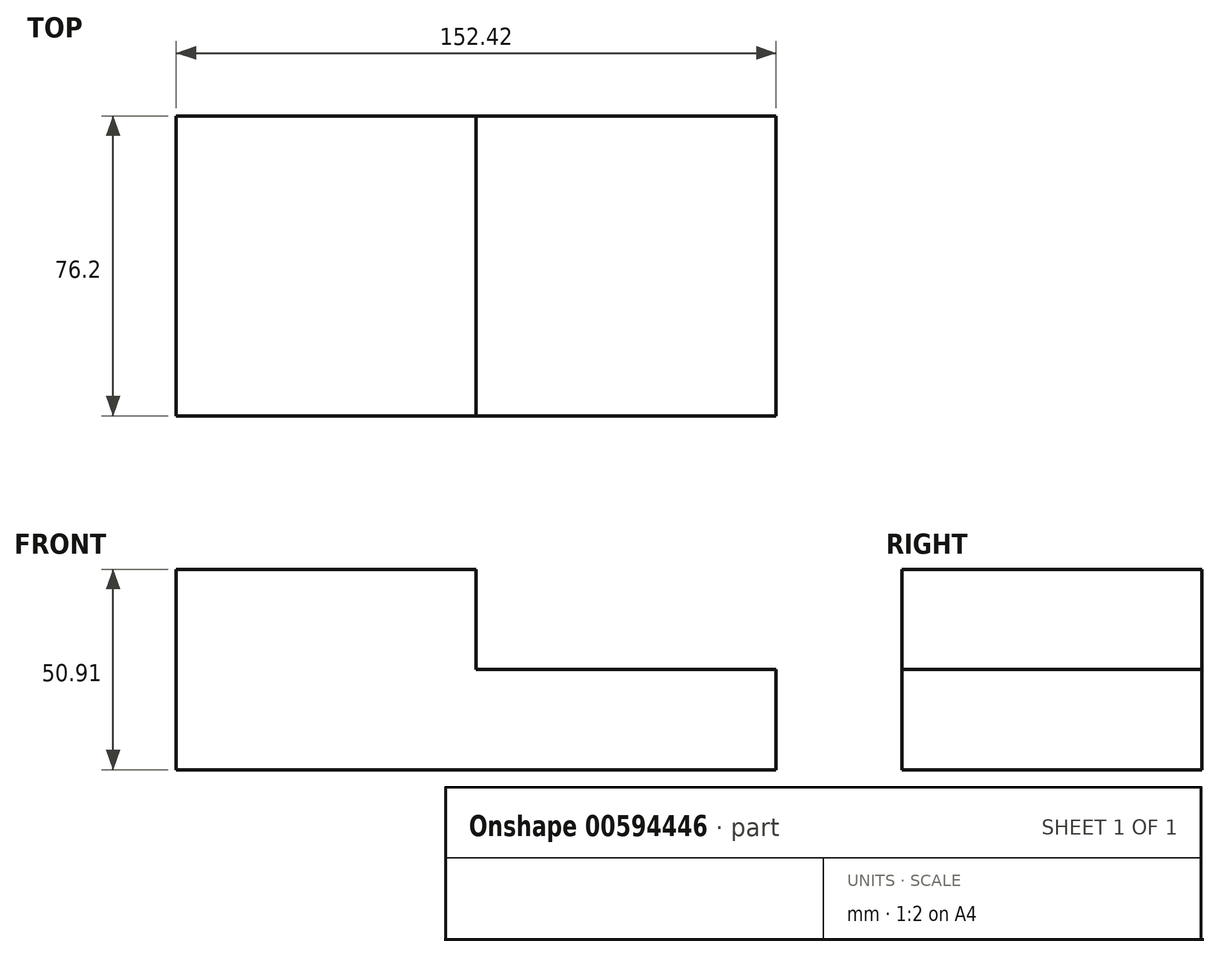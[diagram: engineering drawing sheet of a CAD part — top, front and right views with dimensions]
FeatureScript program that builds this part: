
annotation { "Feature Type Name" : "Feature", "Feature Type Description" : "" }
export const myFeature = defineFeature(function(context is Context, id is Id, definition is map)
    precondition{}
    {
        {
            var Q0;
            Q0=qCreatedBy(makeId("Front.planeOp"),FACE);
            var sketch = newSketch(context, id + "F0", { "sketchPlane" : qUnion([Q0])});
            skLineSegment(sketch, "E0", {"start": v(0, 0) * mm, "end": v(-76.21, 0) * mm});
            skLineSegment(sketch, "E1", {"start": v(0, 0) * mm, "end": v(76.21, 0) * mm});
            skLineSegment(sketch, "E2", {"start": v(-76.21, 0) * mm, "end": v(-76.21, 50.9) * mm});
            skLineSegment(sketch, "E3", {"start": v(-76.21, 50.9) * mm, "end": v(0, 50.9) * mm});
            skLineSegment(sketch, "E4", {"start": v(0, 50.9) * mm, "end": v(0, 25.4) * mm});
            skLineSegment(sketch, "E5", {"start": v(0, 25.4) * mm, "end": v(76.21, 25.4) * mm});
            skLineSegment(sketch, "E6", {"start": v(76.21, 25.4) * mm, "end": v(76.21, 0) * mm});
            skSolve(sketch);
        }
        {
            var Q0;
            Q0=makeQuery(id+"F0.imprint","IMPRINT",FACE,{"disambiguationData":[TD([[makeQuery(id+"F0.imprint","IMPRINT",EDGE,{"derivedFrom":sQuery(id+"F0.wireOp",EDGE,"E0")}),-1.0]])]});
            extrude(context, id + "F1", {"entities" : qUnion([Q0]), "depth" : 76.2 * mm, "offsetDistance" : 25.4 * mm});
        }
    });
